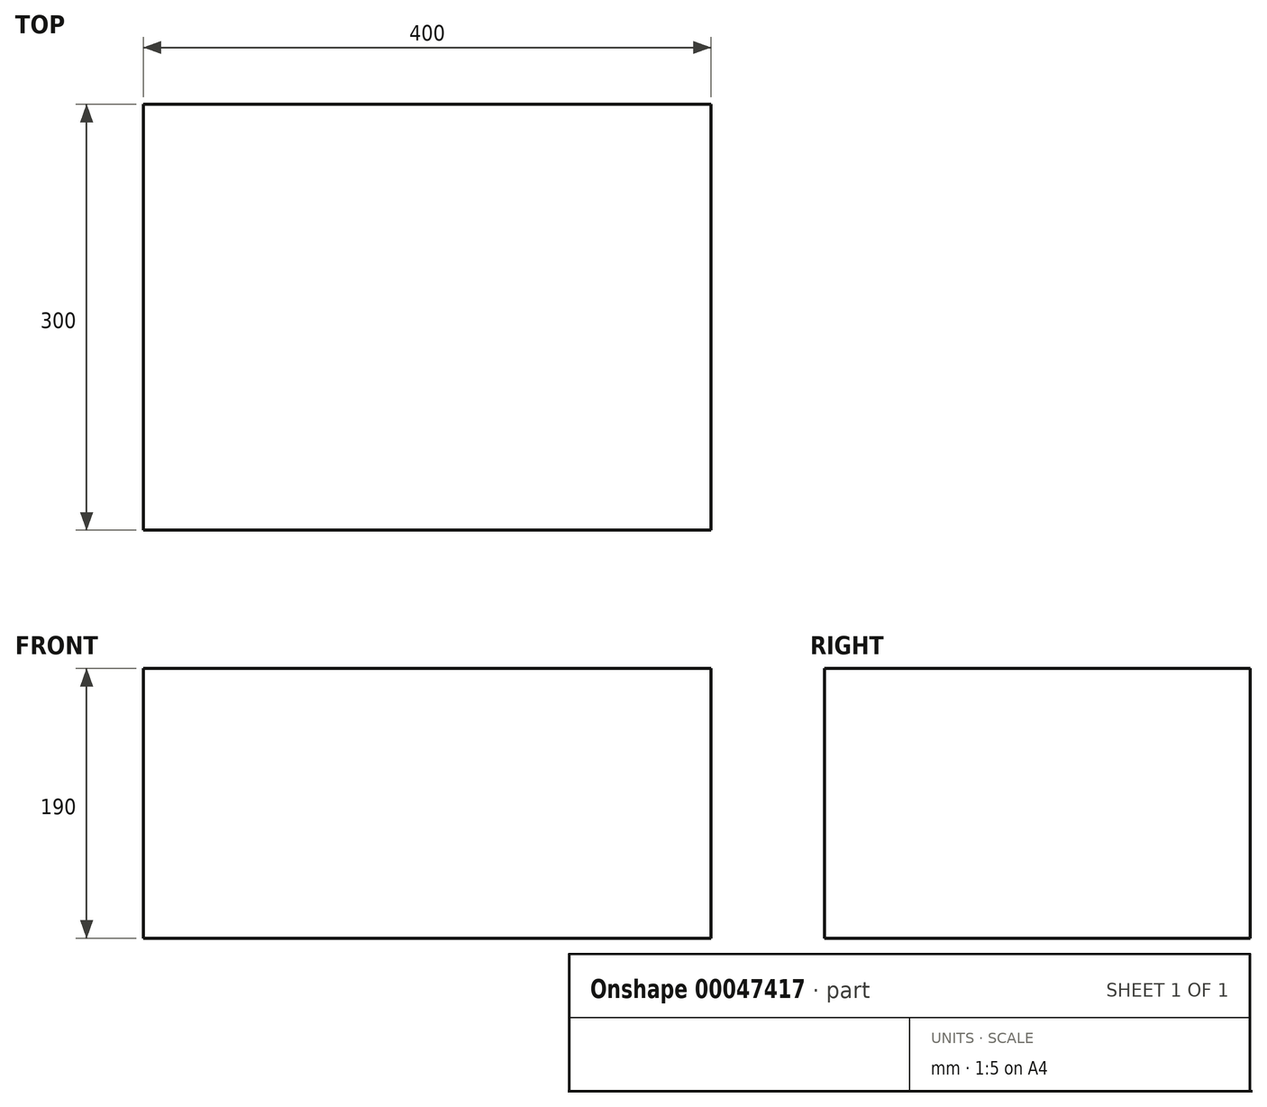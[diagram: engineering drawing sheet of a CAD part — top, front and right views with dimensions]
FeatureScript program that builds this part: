
annotation { "Feature Type Name" : "Feature", "Feature Type Description" : "" }
export const myFeature = defineFeature(function(context is Context, id is Id, definition is map)
    precondition{}
    {
        {
            var Q0;
            Q0=qCreatedBy(makeId("Top.planeOp"),FACE);
            var sketch = newSketch(context, id + "F0", { "sketchPlane" : qUnion([Q0])});
            skLineSegment(sketch, "E0.rect.bottom", {"start": v(200, -150) * mm, "end": v(-200, -150) * mm});
            skLineSegment(sketch, "E0.rect.top", {"start": v(200, 150) * mm, "end": v(-200, 150) * mm});
            skLineSegment(sketch, "E0.rect.left", {"start": v(200, -150) * mm, "end": v(200, 150) * mm});
            skLineSegment(sketch, "E0.rect.right", {"start": v(-200, -150) * mm, "end": v(-200, 150) * mm});
            skPoint(sketch, "E0.rect.middle", {"position": v(0, 0) * mm});
            skSolve(sketch);
        }
        {
            var Q0;
            Q0 = qSketchRegion(id + "F0", true);
            extrude(context, id + "F1", {"entities" : qUnion([Q0]), "depth" : 190 * mm});
        }
    });
